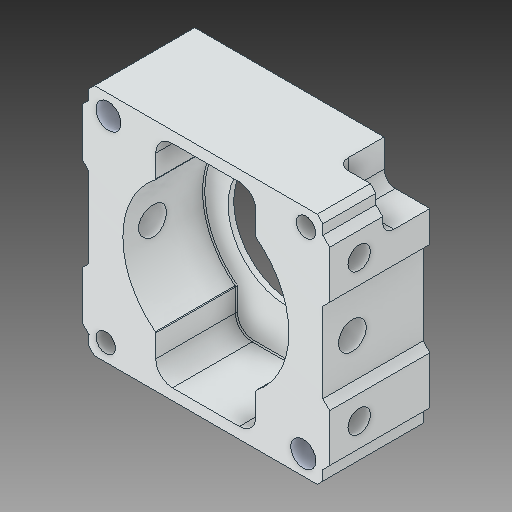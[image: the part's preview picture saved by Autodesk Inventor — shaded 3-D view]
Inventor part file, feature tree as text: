
AUTODESK INVENTOR PART (.ipt)
format: ipt  version: 2017 SP1 (Build 210196100, 196)  size: 267,776 bytes
history: native  units: in
note: dims shown in document units (in); Inventor stores cm internally (conversion verified against a paired STEP export)
features: chamfer x1
ambient origin geometry x8: Origin, YZ Plane, XZ Plane, XY Plane, X Axis, Y Axis, Z Axis, Center Point
bodies: Solid1 (feature_tree)
feature tree (1):
  chamfer  "Chamfer4"  [1 undecoded]
note: 1 required parameter value undecoded (feature->parameter linkage not recoverable at this tier; creation-order binding heuristic only, values carry confidence <= 0.55)
